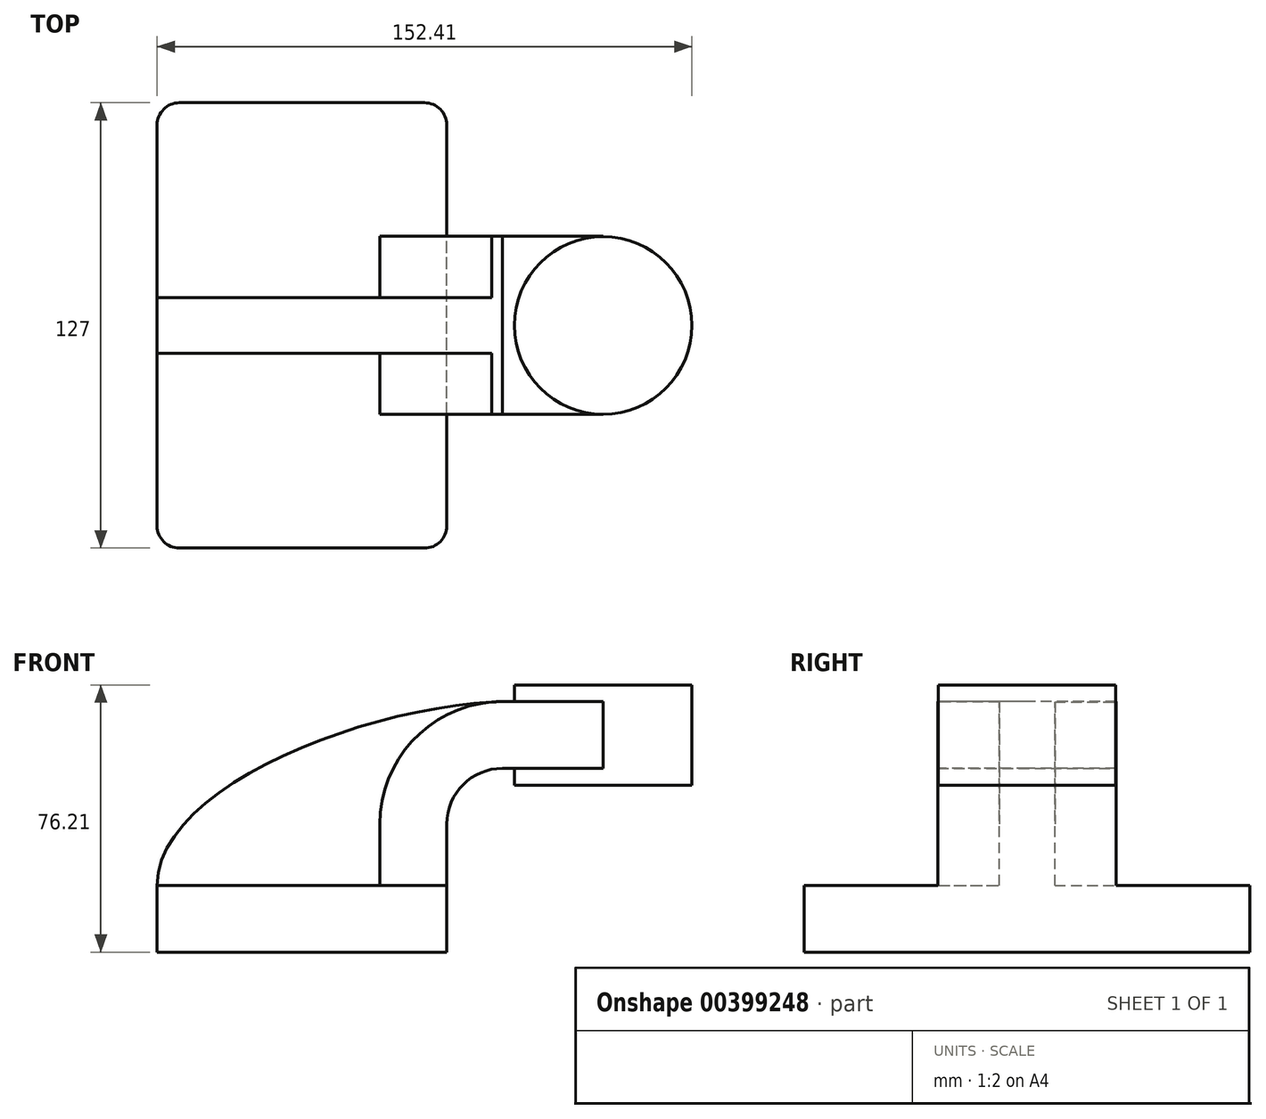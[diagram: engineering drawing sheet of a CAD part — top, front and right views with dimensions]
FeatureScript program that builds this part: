
annotation { "Feature Type Name" : "Feature", "Feature Type Description" : "" }
export const myFeature = defineFeature(function(context is Context, id is Id, definition is map)
    precondition{}
    {
        {
            var Q0;
            Q0=qCreatedBy(makeId("Front.planeOp"),FACE);
            var sketch = newSketch(context, id + "F0", { "sketchPlane" : qUnion([Q0])});
            skLineSegment(sketch, "E0.bottom", {"start": v(41.28, -9.52) * mm, "end": v(-41.28, -9.53) * mm});
            skLineSegment(sketch, "E0.top", {"start": v(41.28, 9.53) * mm, "end": v(-41.28, 9.53) * mm});
            skLineSegment(sketch, "E0.left", {"start": v(41.28, -9.52) * mm, "end": v(41.28, 9.53) * mm});
            skLineSegment(sketch, "E0.right", {"start": v(-41.28, -9.53) * mm, "end": v(-41.28, 9.53) * mm});
            skPoint(sketch, "E0.middle", {"position": v(0, 0) * mm});
            skLineSegment(sketch, "E1.bottom", {"start": v(111.12, 38.1) * mm, "end": v(60.32, 38.1) * mm});
            skLineSegment(sketch, "E1.top", {"start": v(111.12, 66.68) * mm, "end": v(60.32, 66.68) * mm});
            skLineSegment(sketch, "E1.left", {"start": v(111.12, 38.1) * mm, "end": v(111.12, 66.68) * mm});
            skLineSegment(sketch, "E1.right", {"start": v(60.32, 38.1) * mm, "end": v(60.32, 66.68) * mm});
            skPoint(sketch, "E1.middle", {"position": v(85.72, 52.39) * mm});
            skLineSegment(sketch, "E2", {"start": v(41.28, 9.53) * mm, "end": v(41.28, 27) * mm});
            skArc(sketch, "E3", {"start": v(41.27, 27) * mm, "mid": v(45.92, 38.23) * mm, "end": v(57.15, 42.88) * mm});
            skLineSegment(sketch, "E4", {"start": v(57.15, 42.88) * mm, "end": v(85.82, 42.88) * mm});
            skLineSegment(sketch, "E5", {"start": v(85.82, 38.1) * mm, "end": v(85.82, 66.68) * mm});
            skLineSegment(sketch, "E6.0", {"start": v(57.15, 61.93) * mm, "end": v(85.82, 61.93) * mm});
            skArc(sketch, "E6.1", {"start": v(22.23, 27) * mm, "mid": v(32.45, 51.7) * mm, "end": v(57.15, 61.93) * mm});
            skLineSegment(sketch, "E6.2", {"start": v(22.22, 9.53) * mm, "end": v(22.22, 27) * mm});
            skFitSpline(sketch, "E7", {"points": [v(-41.28, 9.52) * mm, v(57.15, 61.93) * mm], "startDerivative": vector(0.64, 85.76) * mm, "endDerivative": vector(114.63, 3.4) * mm});
            skSolve(sketch);
        }
        {
            var Q0;
            Q0=makeQuery(id+"F0.imprint","IMPRINT",FACE,{"disambiguationData":[TD([[makeQuery(id+"F0.imprint","IMPRINT",EDGE,{"derivedFrom":sQuery(id+"F0.wireOp",EDGE,"E0.bottom")}),-1.0]])]});
            extrude(context, id + "F1", {"entities" : qUnion([Q0]), "endBound" : BoundingType.SYMMETRIC, "depth" : 127 * mm});
        }
        {
            var Q0;
            {var subQ1=sQuery(id+"F0.wireOp",EDGE,"E2");Q0=makeQuery(id+"F0.imprint","IMPRINT",FACE,{"disambiguationData":[TD([[makeQuery(id+"F0.imprint","IMPRINT",EDGE,{"derivedFrom":subQ1}),1.0]])]});}
            var Q1;
            {var subQ0=sQuery(id+"F0.wireOp",EDGE,"E4");var subQ1=sQuery(id+"F0.wireOp",EDGE,"E1.right");var subQ2=makeQuery(id+"F0.imprint","INTERSECT",VERTEX,{"derivedFrom":[subQ1,subQ0]});Q1=makeQuery(id+"F0.imprint","IMPRINT",FACE,{"disambiguationData":[TD([[makeQuery(id+"F0.imprint","IMPRINT",EDGE,{"disambiguationData":[TD([[subQ2,-1.0]])],"derivedFrom":subQ1}),-1.0]])]});}
            extrude(context, id + "F2", {"entities" : qUnion([Q0, Q1]), "operationType" : NewBodyOperationType.ADD, "endBound" : BoundingType.SYMMETRIC, "depth" : 50.8 * mm});
        }
        {
            var Q0;
            {var subQ3=sQuery(id+"F0.wireOp",EDGE,"E6.2");Q0=makeQuery(id+"F0.imprint","IMPRINT",FACE,{"disambiguationData":[TD([[makeQuery(id+"F0.imprint","IMPRINT",EDGE,{"derivedFrom":subQ3}),1.0]])]});}
            extrude(context, id + "F3", {"entities" : qUnion([Q0]), "operationType" : NewBodyOperationType.ADD, "endBound" : BoundingType.SYMMETRIC, "depth" : 15.88 * mm});
        }
        {
            var Q0;
            {var subQ0=sQuery(id+"F0.wireOp",EDGE,"E1.left");Q0=makeQuery(id+"F0.imprint","IMPRINT",FACE,{"disambiguationData":[TD([[makeQuery(id+"F0.imprint","IMPRINT",EDGE,{"derivedFrom":subQ0}),1.0]])]});}
            var Q1;
            Q1=sQuery(id+"F0.wireOp",EDGE,"E5");
            revolve(context, id + "F4", {"operationType" : NewBodyOperationType.ADD, "entities" : qUnion([Q0]), "axis" : qUnion([Q1]), "revolveType" : RevolveType.FULL});
        }
        {
            var Q0;
            Q0=makeQuery(id+"F1.opExtrude","CAP_EDGE",EDGE,{"disambiguationData":[OSD([sQuery(id+"F0.wireOp",EDGE,"E0.right")])],"isStart":false});
            var Q1;
            Q1=makeQuery(id+"F1.opExtrude","CAP_EDGE",EDGE,{"disambiguationData":[OSD([sQuery(id+"F0.wireOp",EDGE,"E0.left")])],"isStart":false});
            var Q2;
            Q2=makeQuery(id+"F1.opExtrude","CAP_EDGE",EDGE,{"disambiguationData":[OSD([sQuery(id+"F0.wireOp",EDGE,"E0.right")])],"isStart":true});
            var Q3;
            Q3=makeQuery(id+"F1.opExtrude","CAP_EDGE",EDGE,{"disambiguationData":[OSD([sQuery(id+"F0.wireOp",EDGE,"E0.left")])],"isStart":true});
            fillet(context, id + "F5", {"entities" : qUnion([Q0, Q1, Q2, Q3]), "radius" : 6.35 * mm, "tangentPropagation" : true, "allowEdgeOverflow" : false});
        }
    });
